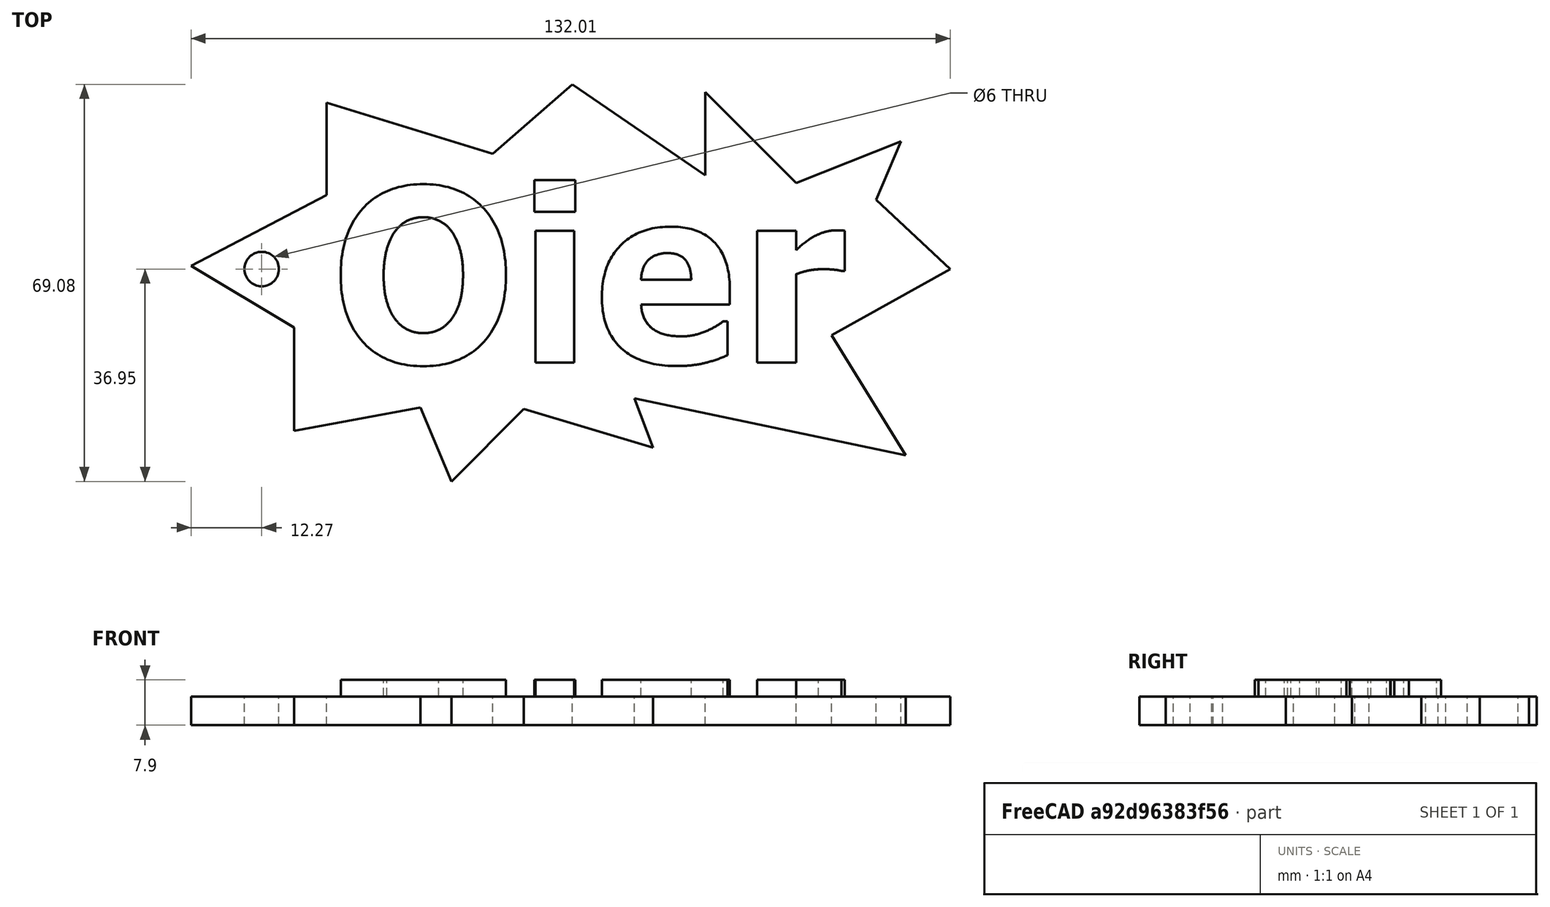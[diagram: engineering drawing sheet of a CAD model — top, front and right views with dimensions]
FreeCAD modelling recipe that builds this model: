
FCSTD DOCUMENT  (FreeCAD 0.16R6706 (Git))
Label: Oier llavero
License: CreativeCommons Attribution-ShareAlike
LicenseURL: http://creativecommons.org/licenses/by-sa/4.0/
objects: Part::Feature×7, Part::Extrusion×7, Part::Cut×3, Part::MultiFuse×2, Sketcher::SketchObject×1, PartDesign::Pad×1, Part::Cylinder×1
note: 23 computed .brp shape members not serialized (recipe doc carries the construction recipe); baked Part::Feature solids carry a one-line shape summary decoded from their .brp

FEATURE [Part::Feature] path58
  shape: bbox 28.76 x 31.66 x 2.09e-07 mm, 0 faces, 0 solids (baked)
FEATURE [Part::Feature] path58001
  shape: bbox 13.81 x 20.19 x 2.09e-07 mm, 0 faces, 0 solids (baked)
FEATURE [Part::Feature] path60
  shape: bbox 6.744 x 22.92 x 2.09e-07 mm, 0 faces, 0 solids (baked)
FEATURE [Part::Feature] path60001
  shape: bbox 7.119 x 5.572 x 2.09e-07 mm, 0 faces, 0 solids (baked)
FEATURE [Part::Feature] path62
  shape: bbox 22.25 x 24.25 x 2.09e-07 mm, 0 faces, 0 solids (baked)
FEATURE [Part::Feature] path62001
  shape: bbox 8.748 x 4.633 x 2.09e-07 mm, 0 faces, 0 solids (baked)
FEATURE [Part::Feature] path64
  shape: bbox 15.25 x 23 x 2.09e-07 mm, 0 faces, 0 solids (baked)
FEATURE [Part::Extrusion] Extrude
  Base = -> path58
  Dir = (0,0,4)
  Solid = true
FEATURE [Part::Extrusion] Extrude001
  Base = -> path58001
  Dir = (0,0,4)
  Solid = true
FEATURE [Part::Extrusion] Extrude002
  Base = -> path60
  Dir = (0,0,4)
  Solid = true
FEATURE [Part::Extrusion] Extrude003
  Base = -> path60001
  Dir = (0,0,4)
  Solid = true
FEATURE [Part::Extrusion] Extrude004
  Base = -> path62
  Dir = (0,0,4)
  Solid = true
FEATURE [Part::Extrusion] Extrude005
  Base = -> path62001
  Dir = (0,0,4)
  Solid = true
FEATURE [Part::Extrusion] Extrude006
  Base = -> path64
  Dir = (0,0,4)
  Solid = true
FEATURE [Part::Cut] Cut
  Base = -> Extrude
  Tool = -> Extrude001
FEATURE [Part::Cut] Cut001
  Base = -> Extrude004
  Tool = -> Extrude005
FEATURE [Part::MultiFuse] Fusion
  Placement = pos=(0.0250047,-0.364427,3.9) rot=(0,0,1;0rad)
  Shapes = -> [Extrude002,Cut,Cut001,Extrude003,Extrude006]
FEATURE [Sketcher::SketchObject] Sketch
  sketch-geometry (20):
    g0: LineSegment StartX=-13.7897 StartY=20.0821 StartZ=0 EndX=-42.7079 EndY=28.9182 EndZ=0
    g1: LineSegment StartX=-42.7079 StartY=28.9182 StartZ=0 EndX=-42.7079 EndY=12.8525 EndZ=0
    g2: LineSegment StartX=-42.7079 StartY=12.8525 StartZ=0 EndX=-66.2709 EndY=0.535526 EndZ=0
    g3: LineSegment StartX=-66.2709 StartY=0.535526 StartZ=0 EndX=-48.3309 EndY=-10.1749 EndZ=0
    g4: LineSegment StartX=-48.3309 StartY=-10.1749 StartZ=0 EndX=-48.3309 EndY=-28.1149 EndZ=0
    g5: LineSegment StartX=-48.3309 StartY=-28.1149 StartZ=0 EndX=-26.3745 EndY=-24.0985 EndZ=0
    g6: LineSegment StartX=-26.3745 StartY=-24.0985 StartZ=0 EndX=-21.0193 EndY=-36.9511 EndZ=0
    g7: LineSegment StartX=-21.0193 StartY=-36.9511 StartZ=0 EndX=-8.43448 EndY=-24.3663 EndZ=0
    g8: LineSegment StartX=-8.43448 StartY=-24.3663 StartZ=0 EndX=14.0575 EndY=-31.0603 EndZ=0
    g9: LineSegment StartX=14.0575 StartY=-31.0603 StartZ=0 EndX=10.8443 EndY=-22.4919 EndZ=0
    g10: LineSegment StartX=10.8443 StartY=-22.4919 StartZ=0 EndX=57.9703 EndY=-32.3991 EndZ=0
    g11: LineSegment StartX=57.9703 StartY=-32.3991 StartZ=0 EndX=45.1178 EndY=-11.5137 EndZ=0
    g12: LineSegment StartX=45.1178 StartY=-11.5137 StartZ=0 EndX=65.7354 EndY=0 EndZ=0
    g13: LineSegment StartX=65.7354 StartY=0 StartZ=0 EndX=52.8829 EndY=12.0493 EndZ=0
    g14: LineSegment StartX=52.8829 StartY=12.0493 StartZ=0 EndX=57.167 EndY=22.2242 EndZ=0
    g15: LineSegment StartX=57.167 StartY=22.2242 StartZ=0 EndX=38.9593 EndY=14.9946 EndZ=0
    g16: LineSegment StartX=38.9593 StartY=14.9946 StartZ=0 EndX=23.1614 EndY=30.7925 EndZ=0
    g17: LineSegment StartX=23.1614 StartY=30.7925 StartZ=0 EndX=23.1614 EndY=16.3334 EndZ=0
    g18: LineSegment StartX=23.1614 StartY=16.3334 StartZ=0 EndX=0 EndY=32.1314 EndZ=0
    g19: LineSegment StartX=0 StartY=32.1314 StartZ=0 EndX=-13.7897 EndY=20.0821 EndZ=0
  constraints (25):
    c: Coincident(g0,g1)
    c: Vertical(g1)
    c: Coincident(g1,g2)
    c: Coincident(g2,g3)
    c: Coincident(g3,g4)
    c: Vertical(g4)
    c: Coincident(g4,g5)
    c: Coincident(g5,g6)
    c: Coincident(g6,g7)
    c: Coincident(g7,g8)
    c: Coincident(g8,g9)
    c: Coincident(g9,g10)
    c: Coincident(g10,g11)
    c: Coincident(g11,g12)
    c: PointOnObject(g12,g-1)
    c: Coincident(g12,g13)
    c: Coincident(g13,g14)
    c: Coincident(g14,g15)
    c: Coincident(g15,g16)
    c: Coincident(g16,g17)
    c: Vertical(g17)
    c: Coincident(g17,g18)
    c: PointOnObject(g18,g-2)
    c: Coincident(g18,g19)
    c: Coincident(g19,g0)
FEATURE [PartDesign::Pad] Pad
  Length = 5
  Length2 = 100
  Sketch = -> Sketch
  Type = 0
FEATURE [Part::Cylinder] Cylinder  label="Cilindro"
  Angle = 360
  Height = 10
  Placement = pos=(-54,0,-2) rot=(0,0,1;0rad)
  Radius = 3
FEATURE [Part::MultiFuse] Fusion001
  Shapes = -> [Pad,Fusion]
FEATURE [Part::Cut] Cut002
  Base = -> Fusion001
  Tool = -> Cylinder
